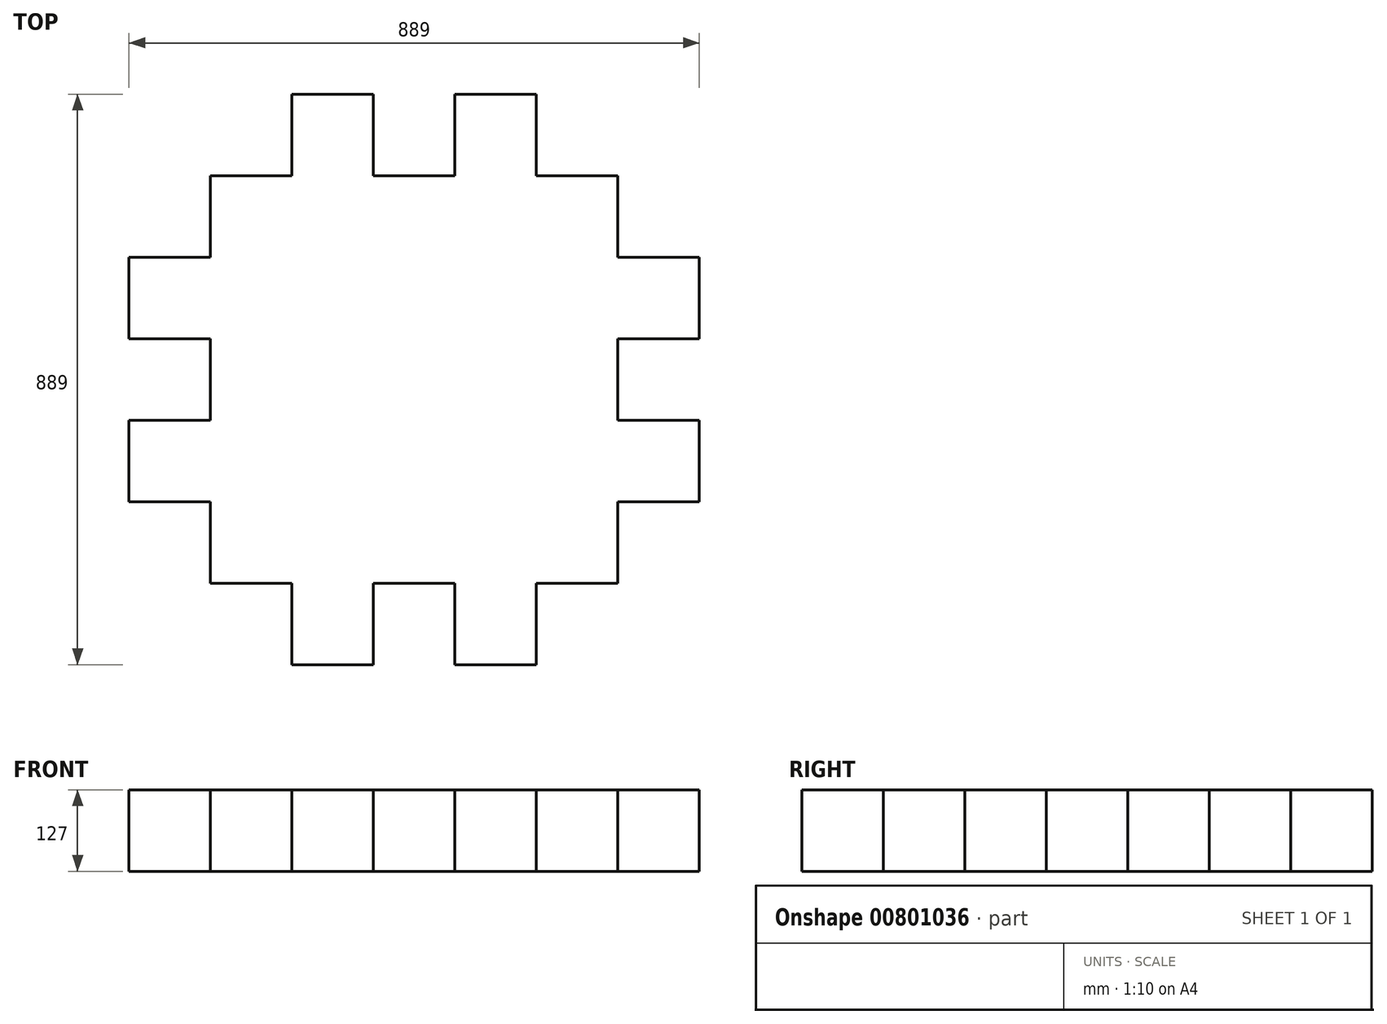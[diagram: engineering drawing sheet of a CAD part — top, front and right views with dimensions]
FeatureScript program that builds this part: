
annotation { "Feature Type Name" : "Feature", "Feature Type Description" : "" }
export const myFeature = defineFeature(function(context is Context, id is Id, definition is map)
    precondition{}
    {
        {
            var Q0;
            Q0=qCreatedBy(makeId("Top.planeOp"),FACE);
            var sketch = newSketch(context, id + "F0", { "sketchPlane" : qUnion([Q0])});
            skLineSegment(sketch, "E0.bottom", {"start": v(0, 0) * mm, "end": v(635, 0) * mm});
            skLineSegment(sketch, "E0.top", {"start": v(0, -635) * mm, "end": v(635, -635) * mm});
            skLineSegment(sketch, "E0.left", {"start": v(0, 0) * mm, "end": v(0, -635) * mm});
            skLineSegment(sketch, "E0.right", {"start": v(635, 0) * mm, "end": v(635, -635) * mm});
            skLineSegment(sketch, "E1.bottom", {"start": v(127, 0) * mm, "end": v(254, 0) * mm});
            skLineSegment(sketch, "E1.top", {"start": v(127, 127) * mm, "end": v(254, 127) * mm});
            skLineSegment(sketch, "E1.left", {"start": v(127, 0) * mm, "end": v(127, 127) * mm});
            skLineSegment(sketch, "E1.right", {"start": v(254, 0) * mm, "end": v(254, 127) * mm});
            skLineSegment(sketch, "E2.bottom", {"start": v(381, 0) * mm, "end": v(508, 0) * mm});
            skLineSegment(sketch, "E2.top", {"start": v(381, 127) * mm, "end": v(508, 127) * mm});
            skLineSegment(sketch, "E2.left", {"start": v(381, 0) * mm, "end": v(381, 127) * mm});
            skLineSegment(sketch, "E2.right", {"start": v(508, 0) * mm, "end": v(508, 127) * mm});
            skLineSegment(sketch, "E3.bottom", {"start": v(635, -127) * mm, "end": v(762, -127) * mm});
            skLineSegment(sketch, "E3.top", {"start": v(635, -254) * mm, "end": v(762, -254) * mm});
            skLineSegment(sketch, "E3.left", {"start": v(635, -127) * mm, "end": v(635, -254) * mm});
            skLineSegment(sketch, "E3.right", {"start": v(762, -127) * mm, "end": v(762, -254) * mm});
            skLineSegment(sketch, "E4.bottom", {"start": v(635, -381) * mm, "end": v(762, -381) * mm});
            skLineSegment(sketch, "E4.top", {"start": v(635, -508) * mm, "end": v(762, -508) * mm});
            skLineSegment(sketch, "E4.left", {"start": v(635, -381) * mm, "end": v(635, -508) * mm});
            skLineSegment(sketch, "E4.right", {"start": v(762, -381) * mm, "end": v(762, -508) * mm});
            skLineSegment(sketch, "E5.bottom", {"start": v(0, -127) * mm, "end": v(-127, -127) * mm});
            skLineSegment(sketch, "E5.top", {"start": v(0, -254) * mm, "end": v(-127, -254) * mm});
            skLineSegment(sketch, "E5.left", {"start": v(0, -127) * mm, "end": v(0, -254) * mm});
            skLineSegment(sketch, "E5.right", {"start": v(-127, -127) * mm, "end": v(-127, -254) * mm});
            skLineSegment(sketch, "E6.bottom", {"start": v(0, -381) * mm, "end": v(-127, -381) * mm});
            skLineSegment(sketch, "E6.top", {"start": v(0, -508) * mm, "end": v(-127, -508) * mm});
            skLineSegment(sketch, "E6.left", {"start": v(0, -381) * mm, "end": v(0, -508) * mm});
            skLineSegment(sketch, "E6.right", {"start": v(-127, -381) * mm, "end": v(-127, -508) * mm});
            skLineSegment(sketch, "E7.bottom", {"start": v(127, -635) * mm, "end": v(254, -635) * mm});
            skLineSegment(sketch, "E7.top", {"start": v(127, -762) * mm, "end": v(254, -762) * mm});
            skLineSegment(sketch, "E7.left", {"start": v(127, -635) * mm, "end": v(127, -762) * mm});
            skLineSegment(sketch, "E7.right", {"start": v(254, -635) * mm, "end": v(254, -762) * mm});
            skLineSegment(sketch, "E8.bottom", {"start": v(381, -635) * mm, "end": v(508, -635) * mm});
            skLineSegment(sketch, "E8.top", {"start": v(381, -762) * mm, "end": v(508, -762) * mm});
            skLineSegment(sketch, "E8.left", {"start": v(381, -635) * mm, "end": v(381, -762) * mm});
            skLineSegment(sketch, "E8.right", {"start": v(508, -635) * mm, "end": v(508, -762) * mm});
            skSolve(sketch);
        }
        {
            var Q0;
            Q0 = qSketchRegion(id + "F0", true);
            extrude(context, id + "F1", {"entities" : qUnion([Q0]), "depth" : 127 * mm, "offsetDistance" : 25.4 * mm});
        }
    });
